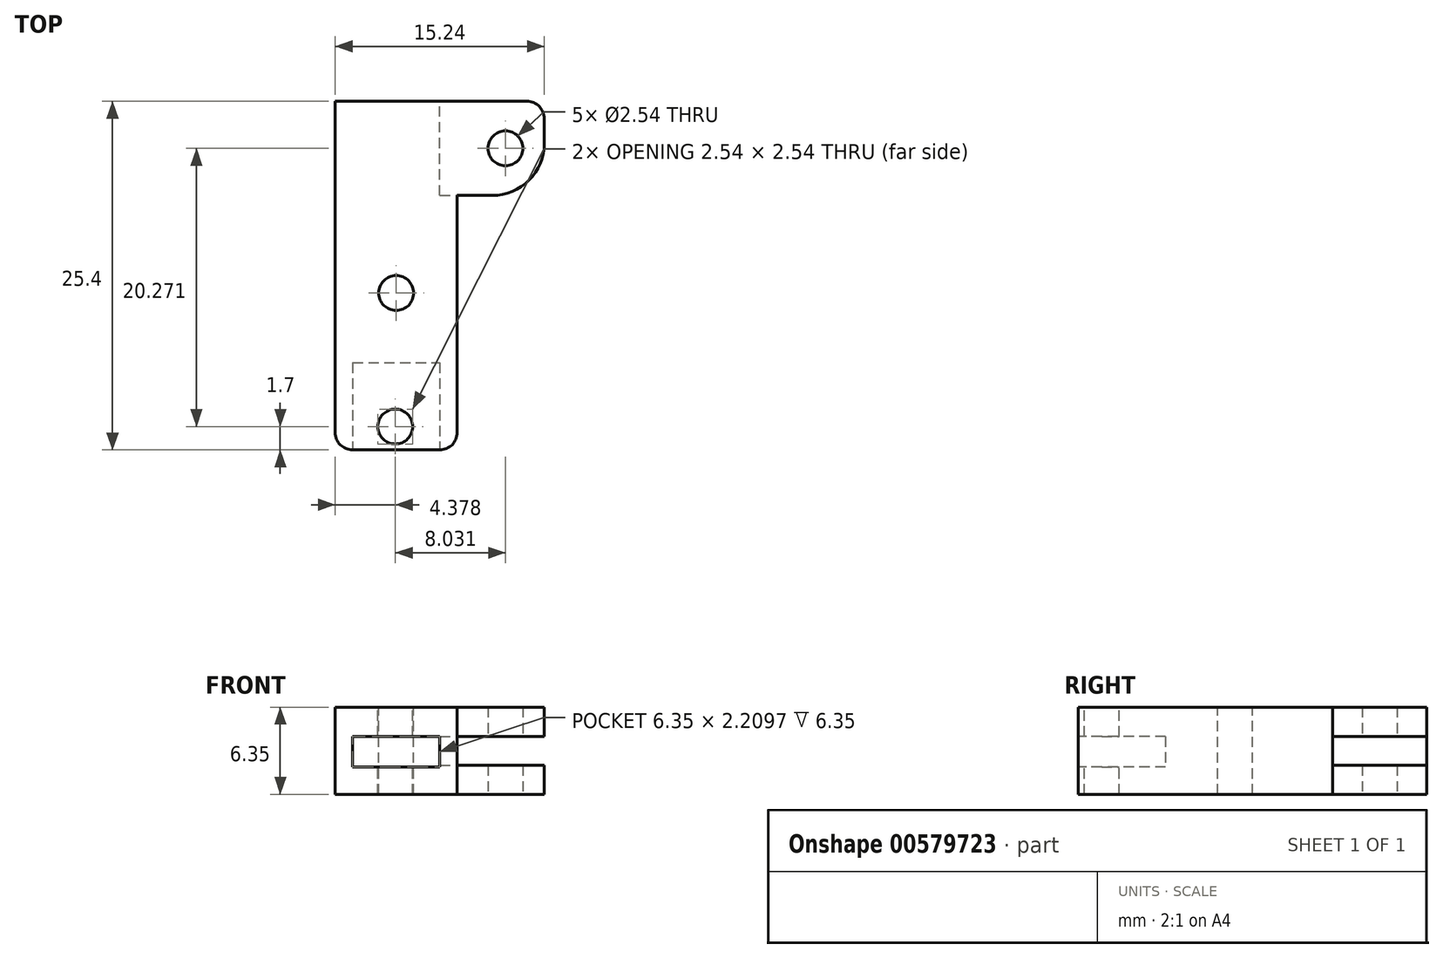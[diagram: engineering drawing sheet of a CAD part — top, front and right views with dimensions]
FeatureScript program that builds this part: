
annotation { "Feature Type Name" : "Feature", "Feature Type Description" : "" }
export const myFeature = defineFeature(function(context is Context, id is Id, definition is map)
    precondition{}
    {
        {
            var Q0;
            Q0=qCreatedBy(makeId("Top.planeOp"),FACE);
            var sketch = newSketch(context, id + "F0", { "sketchPlane" : qUnion([Q0])});
            skLineSegment(sketch, "E0.bottom", {"start": v(0, 0) * mm, "end": v(-8.9, 0) * mm});
            skLineSegment(sketch, "E0.top", {"start": v(0, -25.4) * mm, "end": v(-8.89, -25.4) * mm});
            skLineSegment(sketch, "E0.left", {"start": v(0, -6.86) * mm, "end": v(0, -25.4) * mm});
            skLineSegment(sketch, "E0.right", {"start": v(-8.9, 0) * mm, "end": v(-8.89, -25.4) * mm});
            skLineSegment(sketch, "E1.bottom", {"start": v(-8.9, 0) * mm, "end": v(6.35, 0) * mm});
            skLineSegment(sketch, "E1.top", {"start": v(0, -6.86) * mm, "end": v(6.35, -6.86) * mm});
            skLineSegment(sketch, "E1.left", {"start": v(-8.9, 0) * mm, "end": v(-8.9, -6.86) * mm});
            skLineSegment(sketch, "E1.right", {"start": v(6.35, 0) * mm, "end": v(6.35, -6.86) * mm});
            skPoint(sketch, "E2.centerSnap0", {"position": v(6.35, -3.43) * mm});
            skPoint(sketch, "E3.centerSnap0", {"position": v(-8.9, -3.43) * mm});
            skCircle(sketch, "E4", {"center": v(3.52, -3.43) * mm, "radius": 1.27 * mm});
            skSolve(sketch);
        }
        {
            var Q0;
            Q0=makeQuery(id+"F0.imprint","IMPRINT",FACE,{"disambiguationData":[TD([[makeQuery(id+"F0.imprint","IMPRINT",EDGE,{"derivedFrom":sQuery(id+"F0.wireOp",EDGE,"E0.top")}),-1.0]])]});
            extrude(context, id + "F1", {"entities" : qUnion([Q0]), "depth" : 6.35 * mm, "offsetDistance" : 25.4 * mm});
        }
        {
            var Q0;
            Q0=makeQuery(id+"F1.opExtrude","CAP_FACE",FACE,{"disambiguationData":[OSD([sQuery(id+"F0.wireOp",EDGE,"E0.top"),sQuery(id+"F0.wireOp",EDGE,"E0.left"),sQuery(id+"F0.wireOp",EDGE,"E0.right"),sQuery(id+"F0.wireOp",EDGE,"E1.bottom"),sQuery(id+"F0.wireOp",EDGE,"E1.top"),sQuery(id+"F0.wireOp",EDGE,"E1.left"),sQuery(id+"F0.wireOp",EDGE,"E1.right")])],"isStart":false});
            var sketch = newSketch(context, id + "F2", { "sketchPlane" : qUnion([Q0])});
            skCircle(sketch, "E5", {"center": v(-5.84, -3.19) * mm, "radius": 3.05 * mm});
            skCircle(sketch, "E6", {"center": v(2.97, -3.43) * mm, "radius": 2.97 * mm});
            skPoint(sketch, "E6.centerSnap0", {"position": v(6.35, -3.43) * mm});
            skSolve(sketch);
        }
        {
            var Q0;
            Q0=makeQuery(id+"F1.opExtrude","SWEPT_FACE",FACE,{"disambiguationData":[OSD([sQuery(id+"F0.wireOp",EDGE,"E1.right")])]});
            var sketch = newSketch(context, id + "F3", { "sketchPlane" : qUnion([Q0])});
            skLineSegment(sketch, "E7.bottom", {"start": v(-6.86, 6.35) * mm, "end": v(0, 6.35) * mm});
            skLineSegment(sketch, "E7.top", {"start": v(-6.86, 4.22) * mm, "end": v(0, 4.22) * mm});
            skLineSegment(sketch, "E7.right", {"start": v(0, 6.35) * mm, "end": v(0, 4.22) * mm});
            skLineSegment(sketch, "E8.bottom", {"start": v(-6.86, 0) * mm, "end": v(0, 0) * mm});
            skLineSegment(sketch, "E8.top", {"start": v(-6.86, 2.1) * mm, "end": v(0, 2.1) * mm});
            skLineSegment(sketch, "E8.left", {"start": v(-6.86, 0) * mm, "end": v(-6.86, 2.1) * mm});
            skLineSegment(sketch, "E8.right", {"start": v(0, 0) * mm, "end": v(0, 2.1) * mm});
            skLineSegment(sketch, "E9.left", {"start": v(-6.86, 2.1) * mm, "end": v(-6.86, 4.22) * mm});
            skLineSegment(sketch, "E9.right", {"start": v(0, 2.1) * mm, "end": v(0, 4.22) * mm});
            skSolve(sketch);
        }
        {
            var Q0;
            Q0=makeQuery(id+"F3.imprint","IMPRINT",FACE,{"disambiguationData":[TD([[makeQuery(id+"F3.imprint","IMPRINT",EDGE,{"derivedFrom":sQuery(id+"F3.wireOp",EDGE,"E8.top")}),1.0]])]});
            extrude(context, id + "F4", {"entities" : qUnion([Q0]), "operationType" : NewBodyOperationType.REMOVE, "oppositeDirection" : true, "depth" : 7.62 * mm, "offsetDistance" : 25.4 * mm});
        }
        {
            var Q0;
            Q0=makeQuery(id+"F1.opExtrude","SWEPT_EDGE",EDGE,{"disambiguationData":[OSD([sQuery(id+"F0.wireOp",EDGE,"E0.top"),sQuery(id+"F0.wireOp",EDGE,"E0.left")])]});
            var Q1;
            Q1=makeQuery(id+"F1.opExtrude","SWEPT_EDGE",EDGE,{"disambiguationData":[OSD([sQuery(id+"F0.wireOp",EDGE,"E0.top"),sQuery(id+"F0.wireOp",EDGE,"E0.right")])]});
            var Q2;
            Q2=makeQuery(id+"F1.opExtrude","SWEPT_EDGE",EDGE,{"disambiguationData":[OSD([sQuery(id+"F0.wireOp",EDGE,"E1.bottom"),sQuery(id+"F0.wireOp",EDGE,"E1.left")])]});
            fillet(context, id + "F5", {"entities" : qUnion([Q0, Q1, Q2]), "radius" : 1.27 * mm, "tangentPropagation" : true, "allowEdgeOverflow" : false});
        }
        {
            var Q0;
            Q0=makeQuery(id+"F1.opExtrude","SWEPT_FACE",FACE,{"disambiguationData":[OSD([sQuery(id+"F0.wireOp",EDGE,"E0.top")])]});
            var sketch = newSketch(context, id + "F6", { "sketchPlane" : qUnion([Q0])});
            skLineSegment(sketch, "E10.bottom", {"start": v(-7.62, 6.35) * mm, "end": v(-1.27, 6.35) * mm});
            skLineSegment(sketch, "E10.top", {"start": v(-7.62, 4.22) * mm, "end": v(-1.27, 4.22) * mm});
            skLineSegment(sketch, "E11.bottom", {"start": v(-7.62, 0) * mm, "end": v(-1.27, 0) * mm});
            skLineSegment(sketch, "E11.top", {"start": v(-7.62, 2) * mm, "end": v(-1.27, 2) * mm});
            skLineSegment(sketch, "E12.left", {"start": v(-7.62, 4.22) * mm, "end": v(-7.62, 2) * mm});
            skLineSegment(sketch, "E12.right", {"start": v(-1.27, 4.22) * mm, "end": v(-1.27, 2) * mm});
            skSolve(sketch);
        }
        {
            var Q0;
            Q0=makeQuery(id+"F6.imprint","IMPRINT",FACE,{"disambiguationData":[TD([[makeQuery(id+"F6.imprint","IMPRINT",EDGE,{"derivedFrom":sQuery(id+"F6.wireOp",EDGE,"E10.top")}),-1.0]])]});
            extrude(context, id + "F7", {"entities" : qUnion([Q0]), "operationType" : NewBodyOperationType.REMOVE, "oppositeDirection" : true, "depth" : 6.35 * mm, "offsetDistance" : 25.4 * mm});
        }
        {
            var Q0;
            {var subQ1=sQuery(id+"F2.wireOp",EDGE,"E5");Q0=makeQuery(id+"F2.imprint","IMPRINT",FACE,{"disambiguationData":[TD([[makeQuery(id+"F2.imprint","IMPRINT",EDGE,{"derivedFrom":subQ1}),-1.0]])]});}
            var sketch = newSketch(context, id + "F8", { "sketchPlane" : qUnion([Q0])});
            skCircle(sketch, "E13", {"center": v(-4.51, -23.7) * mm, "radius": 1.27 * mm});
            skSolve(sketch);
        }
        {
            var Q0;
            Q0=sQuery(id+"F8.wireOp",VERTEX,"E13.center");
            var Q1;
            Q1=makeQuery(id+"F1.opExtrude","SWEPT_BODY",BODY,{"disambiguationData":[OSD([sQuery(id+"F0.wireOp",EDGE,"E0.top"),sQuery(id+"F0.wireOp",EDGE,"E0.left"),sQuery(id+"F0.wireOp",EDGE,"E0.right"),sQuery(id+"F0.wireOp",EDGE,"E1.bottom"),sQuery(id+"F0.wireOp",EDGE,"E1.top"),sQuery(id+"F0.wireOp",EDGE,"E1.left"),sQuery(id+"F0.wireOp",EDGE,"E1.right"),sQuery(id+"F0.wireOp",EDGE,"E4"),sQuery(id+"F0.wireOp",EDGE,"uqoV7vl3-qCxJ-rntR-sDxh-xrIGMEDF49GK")])]});
            hole(context, id + "F9", {"style" : HoleStyle.C_BORE, "endStyle" : HoleEndStyle.THROUGH, "holeDiameter" : 2.54 * mm, "cBoreDiameter" : 2.54 * mm, "cBoreDepth" : 6.35 * mm, "majorDiameter" : 6.35 * mm, "isTappedThrough" : true, "tappedDepth" : 12.7 * mm, "tapClearance" : 3, "startFromSketch" : true, "locations" : qUnion([Q0]), "scope" : qUnion([Q1])});
        }
        {
            var Q0;
            {var subQ1=sQuery(id+"F2.wireOp",EDGE,"E5");Q0=makeQuery(id+"F2.imprint","IMPRINT",FACE,{"disambiguationData":[TD([[makeQuery(id+"F2.imprint","IMPRINT",EDGE,{"derivedFrom":subQ1}),-1.0]])]});}
            var sketch = newSketch(context, id + "F10", { "sketchPlane" : qUnion([Q0])});
            skLineSegment(sketch, "E14", {"start": v(0, 0) * mm, "end": v(-4.45, 0) * mm});
            skLineSegment(sketch, "E15", {"start": v(-4.45, 0) * mm, "end": v(-4.45, -13.97) * mm});
            skCircle(sketch, "E16", {"center": v(-4.44, -13.97) * mm, "radius": 1.27 * mm});
            skSolve(sketch);
        }
        {
            var Q0;
            Q0=sQuery(id+"F10.wireOp",VERTEX,"E16.center");
            var Q1;
            Q1=makeQuery(id+"F1.opExtrude","SWEPT_BODY",BODY,{"disambiguationData":[OSD([sQuery(id+"F0.wireOp",EDGE,"E0.top"),sQuery(id+"F0.wireOp",EDGE,"E0.left"),sQuery(id+"F0.wireOp",EDGE,"E0.right"),sQuery(id+"F0.wireOp",EDGE,"E1.bottom"),sQuery(id+"F0.wireOp",EDGE,"E1.top"),sQuery(id+"F0.wireOp",EDGE,"E1.left"),sQuery(id+"F0.wireOp",EDGE,"E1.right"),sQuery(id+"F0.wireOp",EDGE,"E4")])]});
            hole(context, id + "F11", {"style" : HoleStyle.C_BORE, "endStyle" : HoleEndStyle.THROUGH, "holeDiameter" : 2.54 * mm, "cBoreDiameter" : 2.54 * mm, "cBoreDepth" : 6.35 * mm, "majorDiameter" : 6.35 * mm, "isTappedThrough" : true, "tappedDepth" : 12.7 * mm, "tapClearance" : 3, "startFromSketch" : true, "locations" : qUnion([Q0]), "scope" : qUnion([Q1])});
        }
        {
            var Q0;
            {var subQ0=sQuery(id+"F0.wireOp",EDGE,"E1.right");var subQ1=sQuery(id+"F0.wireOp",EDGE,"E1.top");Q0=makeQuery(id+"F4.boolean.opBoolean","SPLIT",EDGE,{"disambiguationData":[TD([makeQuery(id+"F4.opExtrude","SWEPT_FACE",FACE,{"disambiguationData":[OSD([sQuery(id+"F3.wireOp",EDGE,"E7.top")])]})])],"derivedFrom":makeQuery(id+"F1.opExtrude","SWEPT_EDGE",EDGE,{"disambiguationData":[OSD([subQ1,subQ0])]})});}
            var Q1;
            {var subQ0=sQuery(id+"F0.wireOp",EDGE,"E1.right");var subQ1=sQuery(id+"F0.wireOp",EDGE,"E1.top");Q1=makeQuery(id+"F4.boolean.opBoolean","SPLIT",EDGE,{"disambiguationData":[TD([makeQuery(id+"F4.opExtrude","SWEPT_FACE",FACE,{"disambiguationData":[OSD([sQuery(id+"F3.wireOp",EDGE,"E8.top")])]})])],"derivedFrom":makeQuery(id+"F1.opExtrude","SWEPT_EDGE",EDGE,{"disambiguationData":[OSD([subQ1,subQ0])]})});}
            var Q2;
            {var subQ0=sQuery(id+"F0.wireOp",EDGE,"E1.right");var subQ1=sQuery(id+"F0.wireOp",EDGE,"E1.bottom");Q2=makeQuery(id+"F4.boolean.opBoolean","SPLIT",EDGE,{"disambiguationData":[TD([makeQuery(id+"F4.opExtrude","SWEPT_FACE",FACE,{"disambiguationData":[OSD([sQuery(id+"F3.wireOp",EDGE,"E8.top")])]})])],"derivedFrom":makeQuery(id+"F1.opExtrude","SWEPT_EDGE",EDGE,{"disambiguationData":[OSD([subQ1,subQ0])]})});}
            var Q3;
            {var subQ0=sQuery(id+"F0.wireOp",EDGE,"E1.right");var subQ1=sQuery(id+"F0.wireOp",EDGE,"E1.bottom");Q3=makeQuery(id+"F4.boolean.opBoolean","SPLIT",EDGE,{"disambiguationData":[TD([makeQuery(id+"F4.opExtrude","SWEPT_FACE",FACE,{"disambiguationData":[OSD([sQuery(id+"F3.wireOp",EDGE,"E7.top")])]})])],"derivedFrom":makeQuery(id+"F1.opExtrude","SWEPT_EDGE",EDGE,{"disambiguationData":[OSD([subQ1,subQ0])]})});}
            fillet(context, id + "F12", {"entities" : qUnion([Q0, Q1, Q2, Q3]), "radius" : 3.8 * mm, "tangentPropagation" : true, "allowEdgeOverflow" : false});
        }
    });
